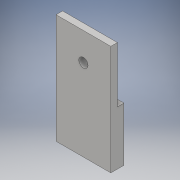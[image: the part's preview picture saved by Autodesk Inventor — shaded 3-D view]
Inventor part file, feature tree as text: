
AUTODESK INVENTOR PART (.ipt)
format: ipt  version: 2017 (Build 210142000, 142)  size: 115,200 bytes
history: native  units: mm
features: extrude x3, sketch x2, hole x2
ambient origin geometry x8: Origin, YZ Plane, XZ Plane, XY Plane, X Axis, Y Axis, Z Axis, Center Point
bodies: Solid1 (feature_tree)
feature tree (7):
  sketch  "Sketch1"  dims[d0=50.0mm d1=25.0mm]
  extrude  "Extrusion1"  Depth=25.0mm
  hole  "Hole1"  [1 undecoded]
  extrude  "Extrusion2"  Depth=3.0mm TaperAngle=0.0deg
  extrude  "Extrusion3"  Depth=3.0mm TaperAngle=0.0deg
  hole  "Hole2"  [1 undecoded]
  sketch  "Sketch2"  dims[d2=25.4mm d3=3.0mm d4=0.0mm d5=4.2mm d6=6.0mm d7=4.0mm d8=2.0mm d9=90.0deg d10=8.0mm d11=20.594885mm d12=3.0mm d13=0.0mm d14=3.0mm d15=0.0mm d16=2.5mm d17=6.0mm d18=4.0mm d19=2.0mm d20=90.0deg d21=10.0mm d22=20.594885mm]
note: 2 required parameter values undecoded (feature->parameter linkage not recoverable at this tier; creation-order binding heuristic only, values carry confidence <= 0.55)
